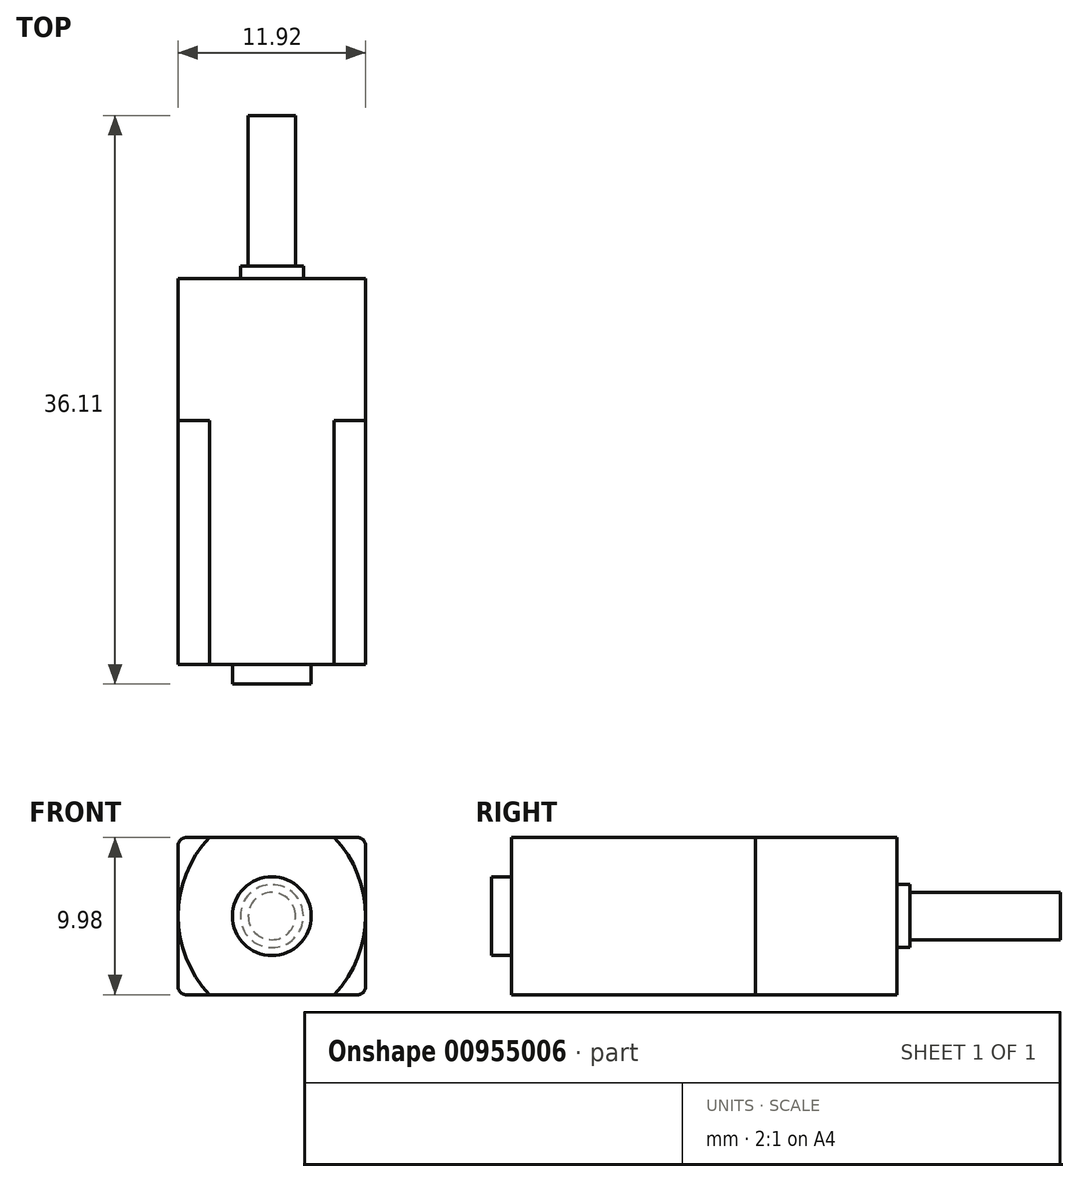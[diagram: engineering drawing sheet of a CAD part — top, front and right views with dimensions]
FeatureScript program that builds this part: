
annotation { "Feature Type Name" : "Feature", "Feature Type Description" : "" }
export const myFeature = defineFeature(function(context is Context, id is Id, definition is map)
    precondition{}
    {
        {
            var Q0;
            Q0=qCreatedBy(makeId("Top.planeOp"),FACE);
            var sketch = newSketch(context, id + "F0", { "sketchPlane" : qUnion([Q0])});
            skLineSegment(sketch, "E0.bottom", {"start": v(-5.96, 7.75) * mm, "end": v(5.96, 7.75) * mm});
            skLineSegment(sketch, "E0.top", {"start": v(-5.96, -7.75) * mm, "end": v(5.95, -7.75) * mm});
            skLineSegment(sketch, "E0.left", {"start": v(-5.96, 7.75) * mm, "end": v(-5.96, -7.75) * mm});
            skLineSegment(sketch, "E0.right", {"start": v(5.96, 7.75) * mm, "end": v(5.95, -7.75) * mm});
            skPoint(sketch, "E0.middle", {"position": v(0, 0) * mm});
            skSolve(sketch);
        }
        {
            var Q0;
            Q0 = qSketchRegion(id + "F0", true);
            extrude(context, id + "F1", {"entities" : qUnion([Q0]), "depth" : 9.98 * mm, "offsetDistance" : 25.4 * mm});
        }
        {
            var Q0;
            Q0=makeQuery(id+"F1.opExtrude","SWEPT_FACE",FACE,{"disambiguationData":[OSD([sQuery(id+"F0.wireOp",EDGE,"E0.top")])]});
            var sketch = newSketch(context, id + "F2", { "sketchPlane" : qUnion([Q0])});
            skArc(sketch, "E1", {"start": v(-3.96, 9.98) * mm, "mid": v(-5.96, 4.99) * mm, "end": v(-3.96, 0) * mm});
            skArc(sketch, "E2.MirrorCS", {"start": v(3.96, 9.98) * mm, "mid": v(5.96, 4.99) * mm, "end": v(3.96, 0) * mm});
            skLineSegment(sketch, "E3", {"start": v(-3.96, 9.98) * mm, "end": v(-7.13, 9.98) * mm});
            skLineSegment(sketch, "E4", {"start": v(-7.13, 9.98) * mm, "end": v(-7.13, 0) * mm});
            skLineSegment(sketch, "E5", {"start": v(-7.13, 0) * mm, "end": v(-3.96, 0) * mm});
            skLineSegment(sketch, "E6", {"start": v(3.96, 0) * mm, "end": v(7.13, 0) * mm});
            skLineSegment(sketch, "E7", {"start": v(7.13, 0) * mm, "end": v(7.13, 9.98) * mm});
            skLineSegment(sketch, "E8", {"start": v(7.13, 9.98) * mm, "end": v(3.96, 9.98) * mm});
            skSolve(sketch);
        }
        {
            var Q0;
            Q0 = qSketchRegion(id + "F2", true);
            extrude(context, id + "F3", {"entities" : qUnion([Q0]), "operationType" : NewBodyOperationType.REMOVE, "oppositeDirection" : true, "depth" : 25.4 * mm, "offsetDistance" : 25.4 * mm});
        }
        {
            var Q0;
            Q0=makeQuery(id+"F1.opExtrude","SWEPT_FACE",FACE,{"disambiguationData":[OSD([sQuery(id+"F0.wireOp",EDGE,"E0.top")])]});
            var sketch = newSketch(context, id + "F4", { "sketchPlane" : qUnion([Q0])});
            skCircle(sketch, "E9", {"center": v(0, 4.99) * mm, "radius": 2.5 * mm});
            skPoint(sketch, "E9.centerSnap0", {"position": v(-5.96, 4.99) * mm});
            skSolve(sketch);
        }
        {
            var Q0;
            Q0 = qSketchRegion(id + "F4", true);
            extrude(context, id + "F5", {"entities" : qUnion([Q0]), "operationType" : NewBodyOperationType.ADD, "depth" : 1.25 * mm, "offsetDistance" : 25.4 * mm});
        }
        {
            var Q0;
            Q0=makeQuery(id+"F1.opExtrude","SWEPT_FACE",FACE,{"disambiguationData":[OSD([sQuery(id+"F0.wireOp",EDGE,"E0.bottom")])]});
            var sketch = newSketch(context, id + "F6", { "sketchPlane" : qUnion([Q0])});
            skLineSegment(sketch, "E10.bottom", {"start": v(-5.96, 9.98) * mm, "end": v(5.96, 9.98) * mm});
            skLineSegment(sketch, "E10.top", {"start": v(-5.96, 0) * mm, "end": v(5.96, 0) * mm});
            skLineSegment(sketch, "E10.left", {"start": v(-5.96, 9.98) * mm, "end": v(-5.96, 0) * mm});
            skLineSegment(sketch, "E10.right", {"start": v(5.96, 9.98) * mm, "end": v(5.96, 0) * mm});
            skPoint(sketch, "E10.middle", {"position": v(0, 5) * mm});
            skPoint(sketch, "E10.middle.positionSnap0", {"position": v(-5.96, 5) * mm});
            skPoint(sketch, "E10.centerSnap0", {"position": v(-5.96, 5) * mm});
            skSolve(sketch);
        }
        {
            var Q0;
            Q0 = qSketchRegion(id + "F6", true);
            extrude(context, id + "F7", {"entities" : qUnion([Q0]), "operationType" : NewBodyOperationType.ADD, "depth" : 9 * mm, "offsetDistance" : 25.4 * mm});
        }
        {
            var Q0;
            Q0=makeQuery(id+"F7.opExtrude","CAP_FACE",FACE,{"disambiguationData":[OSD([sQuery(id+"F6.wireOp",EDGE,"E10.bottom"),sQuery(id+"F6.wireOp",EDGE,"E10.top"),sQuery(id+"F6.wireOp",EDGE,"E10.left"),sQuery(id+"F6.wireOp",EDGE,"E10.right")])],"isStart":false});
            var sketch = newSketch(context, id + "F8", { "sketchPlane" : qUnion([Q0])});
            skCircle(sketch, "E11", {"center": v(0, 5) * mm, "radius": 2 * mm});
            skPoint(sketch, "E11.centerSnap0", {"position": v(-5.96, 5) * mm});
            skSolve(sketch);
        }
        {
            var Q0;
            Q0 = qSketchRegion(id + "F8", true);
            extrude(context, id + "F9", {"entities" : qUnion([Q0]), "operationType" : NewBodyOperationType.ADD, "depth" : .81 * mm, "offsetDistance" : 25.4 * mm});
        }
        {
            var Q0;
            Q0=makeQuery(id+"F9.opExtrude","CAP_FACE",FACE,{"disambiguationData":[OSD([sQuery(id+"F8.wireOp",EDGE,"E11")])],"isStart":false});
            var sketch = newSketch(context, id + "F10", { "sketchPlane" : qUnion([Q0])});
            skCircle(sketch, "E12", {"center": v(0, 5) * mm, "radius": 1.5 * mm});
            skSolve(sketch);
        }
        {
            var Q0;
            Q0 = qSketchRegion(id + "F10", true);
            extrude(context, id + "F11", {"entities" : qUnion([Q0]), "operationType" : NewBodyOperationType.ADD, "depth" : 9.55 * mm, "offsetDistance" : 25.4 * mm});
        }
        {
            var Q0;
            Q0=makeQuery(id+"F7.opExtrude","SWEPT_EDGE",EDGE,{"disambiguationData":[OSD([sQuery(id+"F6.wireOp",EDGE,"E10.bottom"),sQuery(id+"F6.wireOp",EDGE,"E10.left")])]});
            var Q1;
            Q1=makeQuery(id+"F7.opExtrude","SWEPT_EDGE",EDGE,{"disambiguationData":[OSD([sQuery(id+"F6.wireOp",EDGE,"E10.bottom"),sQuery(id+"F6.wireOp",EDGE,"E10.right")])]});
            var Q2;
            Q2=makeQuery(id+"F7.opExtrude","SWEPT_EDGE",EDGE,{"disambiguationData":[OSD([sQuery(id+"F6.wireOp",EDGE,"E10.top"),sQuery(id+"F6.wireOp",EDGE,"E10.left")])]});
            var Q3;
            Q3=makeQuery(id+"F7.opExtrude","SWEPT_EDGE",EDGE,{"disambiguationData":[OSD([sQuery(id+"F6.wireOp",EDGE,"E10.top"),sQuery(id+"F6.wireOp",EDGE,"E10.right")])]});
            fillet(context, id + "F12", {"entities" : qUnion([Q0, Q1, Q2, Q3]), "radius" : .5 * mm, "tangentPropagation" : true, "allowEdgeOverflow" : false});
        }
    });
